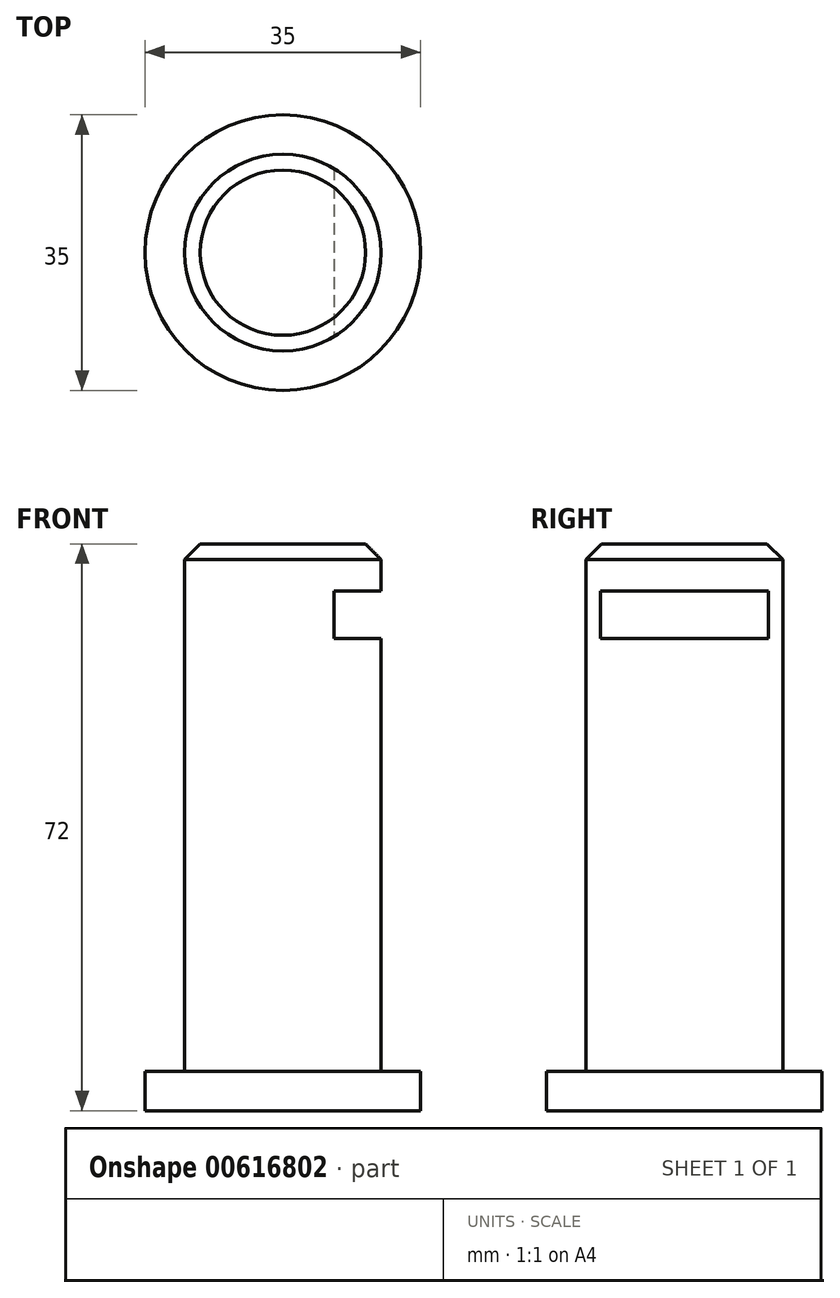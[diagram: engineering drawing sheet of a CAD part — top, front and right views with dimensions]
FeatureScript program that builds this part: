
annotation { "Feature Type Name" : "Feature", "Feature Type Description" : "" }
export const myFeature = defineFeature(function(context is Context, id is Id, definition is map)
    precondition{}
    {
        {
            var Q0;
            Q0=qCreatedBy(makeId("Top.planeOp"),FACE);
            var sketch = newSketch(context, id + "F0", { "sketchPlane" : qUnion([Q0])});
            skCircle(sketch, "E0", {"center": v(0, 0) * mm, "radius": 17.5 * mm});
            skSolve(sketch);
        }
        {
            var Q0;
            Q0 = qSketchRegion(id + "F0", true);
            extrude(context, id + "F1", {"entities" : qUnion([Q0]), "depth" : 5 * mm, "offsetDistance" : 25 * mm});
        }
        {
            var Q0;
            Q0=qCreatedBy(makeId("Top.planeOp"),FACE);
            var sketch = newSketch(context, id + "F2", { "sketchPlane" : qUnion([Q0])});
            skCircle(sketch, "E1", {"center": v(0, 0) * mm, "radius": 12.5 * mm});
            skSolve(sketch);
        }
        {
            var Q0;
            Q0 = qSketchRegion(id + "F2", true);
            extrude(context, id + "F3", {"entities" : qUnion([Q0]), "operationType" : NewBodyOperationType.ADD, "depth" : 72 * mm, "offsetDistance" : 25 * mm});
        }
        {
            var Q0;
            Q0=qCreatedBy(makeId("Front.planeOp"),FACE);
            var sketch = newSketch(context, id + "F4", { "sketchPlane" : qUnion([Q0])});
            skLineSegment(sketch, "E2.bottom", {"start": v(6.5, 66) * mm, "end": v(16.5, 66) * mm});
            skLineSegment(sketch, "E2.top", {"start": v(6.5, 60) * mm, "end": v(16.5, 60) * mm});
            skLineSegment(sketch, "E2.left", {"start": v(6.5, 66) * mm, "end": v(6.5, 60) * mm});
            skLineSegment(sketch, "E2.right", {"start": v(16.5, 66) * mm, "end": v(16.5, 60) * mm});
            skLineSegment(sketch, "E3", {"start": v(-12.5, 5) * mm, "end": v(-12.5, 72) * mm, "construction": true});
            skSolve(sketch);
        }
        {
            var Q0;
            Q0 = qSketchRegion(id + "F4", true);
            extrude(context, id + "F5", {"entities" : qUnion([Q0]), "operationType" : NewBodyOperationType.REMOVE, "endBound" : BoundingType.THROUGH_ALL, "oppositeDirection" : true, "depth" : 25 * mm, "offsetDistance" : 25 * mm, "hasSecondDirection" : true, "secondDirectionBound" : BoundingType.THROUGH_ALL, "secondDirectionOppositeDirection" : false, "secondDirectionDepth" : 25 * mm});
        }
        {
            var Q0;
            Q0=makeQuery(id+"F3.opExtrude","CAP_EDGE",EDGE,{"disambiguationData":[OSD([sQuery(id+"F2.wireOp",EDGE,"E1")])],"isStart":false});
            chamfer(context, id + "F6", {"entities" : qUnion([Q0]), "chamferType" : ChamferType.OFFSET_ANGLE, "width" : 2 * mm, "oppositeDirection" : false, "angle" : 45 * degree, "tangentPropagation" : true});
        }
    });
